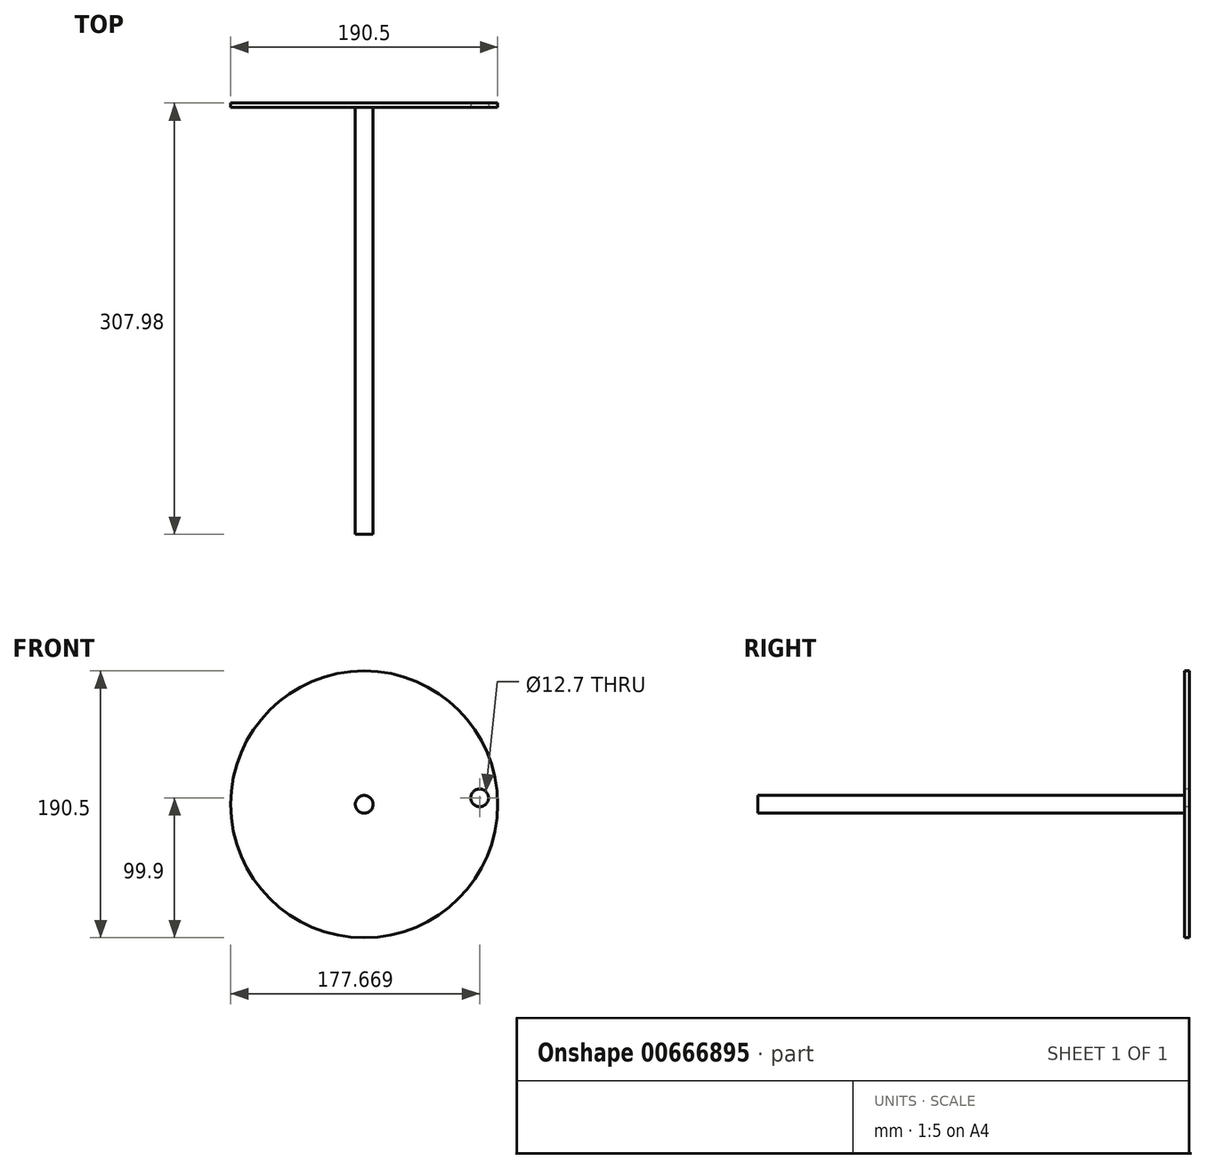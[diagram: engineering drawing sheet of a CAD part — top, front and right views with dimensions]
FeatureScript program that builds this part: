
annotation { "Feature Type Name" : "Feature", "Feature Type Description" : "" }
export const myFeature = defineFeature(function(context is Context, id is Id, definition is map)
    precondition{}
    {
        {
            var Q0;
            Q0=qCreatedBy(makeId("Front.planeOp"),FACE);
            var sketch = newSketch(context, id + "F0", { "sketchPlane" : qUnion([Q0])});
            skCircle(sketch, "E0", {"center": v(0, 0) * mm, "radius": 95.25 * mm});
            skCircle(sketch, "E1", {"center": v(0, 0) * mm, "radius": 82.55 * mm, "construction": true});
            skPoint(sketch, "E2", {"position": v(82.42, 4.65) * mm});
            skCircle(sketch, "E3", {"center": v(82.42, 4.65) * mm, "radius": 6.35 * mm});
            skCircle(sketch, "E4", {"center": v(0, 0) * mm, "radius": 6.35 * mm});
            skSolve(sketch);
        }
        {
            var Q0;
            Q0=makeQuery(id+"F0.imprint","IMPRINT",FACE,{"disambiguationData":[TD([[makeQuery(id+"F0.imprint","IMPRINT",EDGE,{"derivedFrom":sQuery(id+"F0.wireOp",EDGE,"E0")}),1.0]])]});
            extrude(context, id + "F1", {"entities" : qUnion([Q0]), "oppositeDirection" : true, "depth" : 3.17 * mm, "offsetDistance" : 25.4 * mm});
        }
        {
            var Q0;
            Q0=makeQuery(id+"F1.opExtrude","CAP_FACE",FACE,{"disambiguationData":[OSD([sQuery(id+"F0.wireOp",EDGE,"E0"),sQuery(id+"F0.wireOp",EDGE,"E3"),sQuery(id+"F0.wireOp",EDGE,"E4")])],"isStart":true});
            var sketch = newSketch(context, id + "F2", { "sketchPlane" : qUnion([Q0])});
            skCircle(sketch, "E5.0", {"center": v(0, 0) * mm, "radius": 6.35 * mm});
            skSolve(sketch);
        }
        {
            var Q0;
            Q0=makeQuery(id+"F2.imprint","IMPRINT",FACE,{"disambiguationData":[TD([[makeQuery(id+"F2.imprint","IMPRINT",EDGE,{"derivedFrom":sQuery(id+"F2.wireOp",EDGE,"E5.0")}),1.0]])]});
            extrude(context, id + "F3", {"entities" : qUnion([Q0]), "operationType" : NewBodyOperationType.ADD, "depth" : 304.8 * mm, "offsetDistance" : 25.4 * mm, "hasSecondDirection" : true, "secondDirectionOppositeDirection" : true, "secondDirectionDepth" : 3.17 * mm});
        }
    });
